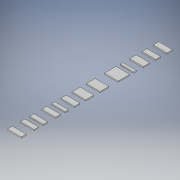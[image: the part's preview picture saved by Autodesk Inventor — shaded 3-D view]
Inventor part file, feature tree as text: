
AUTODESK INVENTOR PART (.ipt)
format: ipt  version: 2017 (Build 210142000, 142)  size: 163,328 bytes
history: native  units: in
note: dims shown in document units (in); Inventor stores cm internally (conversion verified against a paired STEP export)
features: extrude x1, sketch x1
ambient origin geometry x8: Origin, YZ Plane, XZ Plane, XY Plane, X Axis, Y Axis, Z Axis, Center Point
bodies: Solid1 (feature_tree)
feature tree (2):
  extrude  "Extrusion1"  Depth=0.9in
  sketch  "Sketch1"  dims[d0=2.5in d1=0.9in d2=0.8in d3=0.8in d4=2.5in d5=0.9in d6=0.6in d7=2.5in d8=1.0in d9=2.5in d10=1.5in d11=2.5in d12=1.6in d13=2.5in d14=2.1in d15=0.5in d16=1.2in d17=0.9in d18=2.5in d19=1.0in d20=0.2in d21=0.0in]
